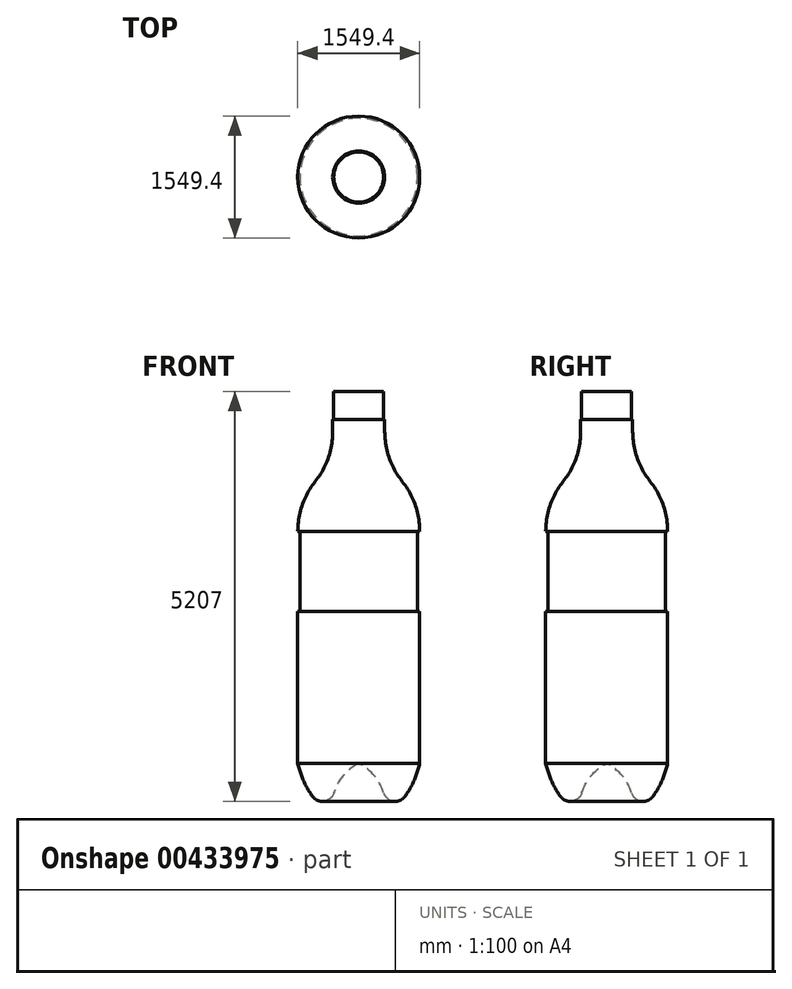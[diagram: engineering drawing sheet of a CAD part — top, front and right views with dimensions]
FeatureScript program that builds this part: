
annotation { "Feature Type Name" : "Feature", "Feature Type Description" : "" }
export const myFeature = defineFeature(function(context is Context, id is Id, definition is map)
    precondition{}
    {
        {
            var Q0;
            Q0=qCreatedBy(makeId("Front.planeOp"),FACE);
            var sketch = newSketch(context, id + "F0", { "sketchPlane" : qUnion([Q0])});
            skLineSegment(sketch, "E0", {"start": v(0, 0) * mm, "end": v(317.5, 0) * mm});
            skLineSegment(sketch, "E1", {"start": v(0, 0) * mm, "end": v(0, -355.6) * mm});
            skLineSegment(sketch, "E2", {"start": v(0, -355.6) * mm, "end": v(-12.7, -355.6) * mm});
            skLineSegment(sketch, "E3", {"start": v(-12.7, -355.6) * mm, "end": v(-12.7, -508) * mm});
            skLineSegment(sketch, "E4", {"start": v(317.5, 0) * mm, "end": v(317.5, -4724.5) * mm});
            skPoint(sketch, "E5", {"position": v(317.5, -4724.5) * mm});
            skArc(sketch, "E6", {"start": v(317.5, -4724.5) * mm, "mid": v(120.9, -4880.37) * mm, "end": v(0, -5100.2) * mm});
            skArc(sketch, "E7", {"start": v(-269.08, -5143.67) * mm, "mid": v(-121.11, -5205.05) * mm, "end": v(0, -5100.2) * mm});
            skArc(sketch, "E8", {"start": v(-457.2, -4724.5) * mm, "mid": v(-384.42, -4943.64) * mm, "end": v(-269.08, -5143.67) * mm});
            skLineSegment(sketch, "E9", {"start": v(-457.2, -4724.5) * mm, "end": v(-457.2, -2792.08) * mm});
            skLineSegment(sketch, "E10", {"start": v(-457.2, -2792.08) * mm, "end": v(-429.26, -2792.08) * mm});
            skLineSegment(sketch, "E11", {"start": v(-429.26, -2792.08) * mm, "end": v(-429.26, -1776.08) * mm});
            skLineSegment(sketch, "E12", {"start": v(-429.26, -1776.08) * mm, "end": v(-457.2, -1776.08) * mm});
            skPoint(sketch, "E13", {"position": v(-457.2, -1776.08) * mm});
            skArc(sketch, "E14", {"start": v(-234.95, -1142.2) * mm, "mid": v(-69.87, -844.01) * mm, "end": v(-12.7, -508) * mm});
            skArc(sketch, "E15", {"start": v(-234.95, -1142.2) * mm, "mid": v(-399.97, -1440.24) * mm, "end": v(-457.2, -1776.08) * mm});
            skPoint(sketch, "E16.orphan", {"position": v(0, -8656.26) * mm});
            skSolve(sketch);
        }
        {
            var Q0;
            Q0=makeQuery(id+"F0.imprint","IMPRINT",FACE,{"disambiguationData":[TD([[makeQuery(id+"F0.imprint","IMPRINT",EDGE,{"derivedFrom":sQuery(id+"F0.wireOp",EDGE,"E0")}),-1.0]])]});
            var Q1;
            Q1=sQuery(id+"F0.wireOp",EDGE,"E4");
            revolve(context, id + "F1", {"entities" : qUnion([Q0]), "axis" : qUnion([Q1]), "revolveType" : RevolveType.FULL});
        }
    });
